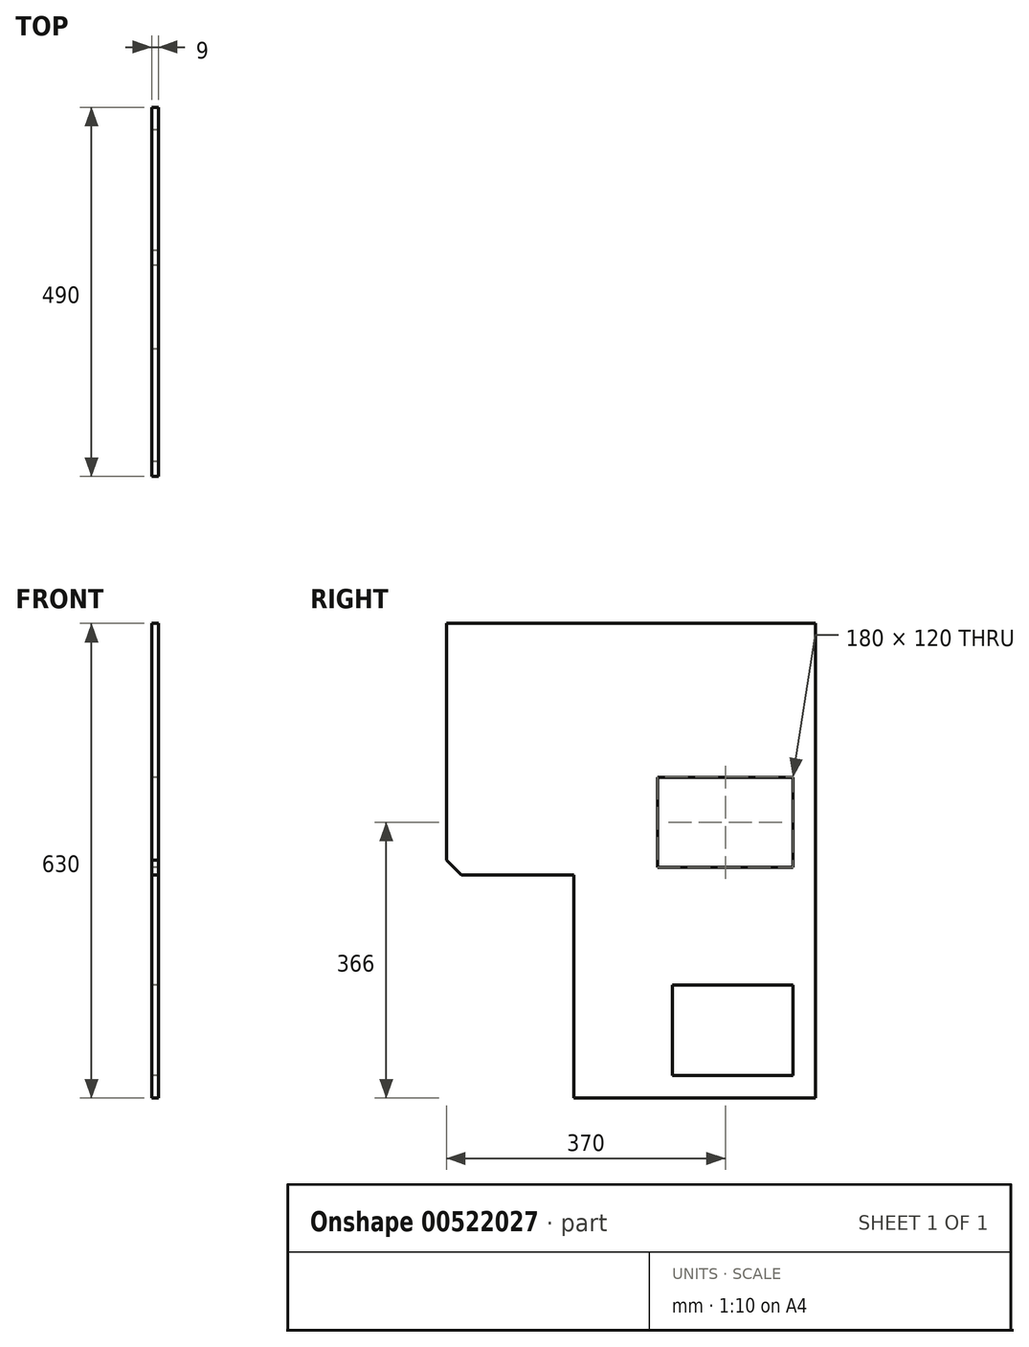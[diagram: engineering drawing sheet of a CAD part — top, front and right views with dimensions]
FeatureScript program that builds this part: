
annotation { "Feature Type Name" : "Feature", "Feature Type Description" : "" }
export const myFeature = defineFeature(function(context is Context, id is Id, definition is map)
    precondition{}
    {
        {
            var Q0;
            Q0=qCreatedBy(makeId("Right.planeOp"),FACE);
            var sketch = newSketch(context, id + "F0", { "sketchPlane" : qUnion([Q0])});
            skLineSegment(sketch, "E0", {"start": v(0, 0) * mm, "end": v(321, 0) * mm});
            skLineSegment(sketch, "E1", {"start": v(321, 0) * mm, "end": v(321, 630) * mm});
            skLineSegment(sketch, "E2", {"start": v(321, 630) * mm, "end": v(-169, 630) * mm});
            skLineSegment(sketch, "E3", {"start": v(-169, 630) * mm, "end": v(-169, 316) * mm});
            skLineSegment(sketch, "E4", {"start": v(-149, 296) * mm, "end": v(0, 296) * mm});
            skLineSegment(sketch, "E5", {"start": v(0, 296) * mm, "end": v(0, 0) * mm});
            skLineSegment(sketch, "E6", {"start": v(-149, 296) * mm, "end": v(-169, 316) * mm});
            skSolve(sketch);
        }
        {
            var Q0;
            Q0=makeQuery(id+"F0.imprint","IMPRINT",FACE,{"disambiguationData":[TD([[makeQuery(id+"F0.imprint","IMPRINT",EDGE,{"derivedFrom":sQuery(id+"F0.wireOp",EDGE,"E0")}),1.0]])]});
            extrude(context, id + "F1", {"entities" : qUnion([Q0]), "depth" : 9 * mm, "offsetDistance" : 25 * mm});
        }
        {
            var Q0;
            Q0=makeQuery(id+"F1.opExtrude","CAP_FACE",FACE,{"disambiguationData":[OSD([sQuery(id+"F0.wireOp",EDGE,"E0"),sQuery(id+"F0.wireOp",EDGE,"E1"),sQuery(id+"F0.wireOp",EDGE,"E2"),sQuery(id+"F0.wireOp",EDGE,"E3"),sQuery(id+"F0.wireOp",EDGE,"E4"),sQuery(id+"F0.wireOp",EDGE,"E5")])],"isStart":true});
            var sketch = newSketch(context, id + "F2", { "sketchPlane" : qUnion([Q0])});
            skLineSegment(sketch, "E7.bottom", {"start": v(-291, 426) * mm, "end": v(-111, 426) * mm});
            skLineSegment(sketch, "E7.top", {"start": v(-291, 306) * mm, "end": v(-111, 306) * mm});
            skLineSegment(sketch, "E7.left", {"start": v(-291, 426) * mm, "end": v(-291, 306) * mm});
            skLineSegment(sketch, "E7.right", {"start": v(-111, 426) * mm, "end": v(-111, 306) * mm});
            skLineSegment(sketch, "E8.bottom", {"start": v(-291, 30) * mm, "end": v(-131, 30) * mm});
            skLineSegment(sketch, "E8.top", {"start": v(-291, 150) * mm, "end": v(-131, 150) * mm});
            skLineSegment(sketch, "E8.left", {"start": v(-291, 30) * mm, "end": v(-291, 150) * mm});
            skLineSegment(sketch, "E8.right", {"start": v(-131, 30) * mm, "end": v(-131, 150) * mm});
            skSolve(sketch);
        }
        {
            var Q0;
            Q0=makeQuery(id+"F2.imprint","IMPRINT",FACE,{"disambiguationData":[TD([[makeQuery(id+"F2.imprint","IMPRINT",EDGE,{"derivedFrom":sQuery(id+"F2.wireOp",EDGE,"E7.bottom")}),-1.0]])]});
            var Q1;
            Q1=makeQuery(id+"F2.imprint","IMPRINT",FACE,{"disambiguationData":[TD([[makeQuery(id+"F2.imprint","IMPRINT",EDGE,{"derivedFrom":sQuery(id+"F2.wireOp",EDGE,"E8.bottom")}),1.0]])]});
            extrude(context, id + "F3", {"entities" : qUnion([Q0, Q1]), "operationType" : NewBodyOperationType.REMOVE, "oppositeDirection" : true, "depth" : 25 * mm, "offsetDistance" : 25 * mm});
        }
    });
